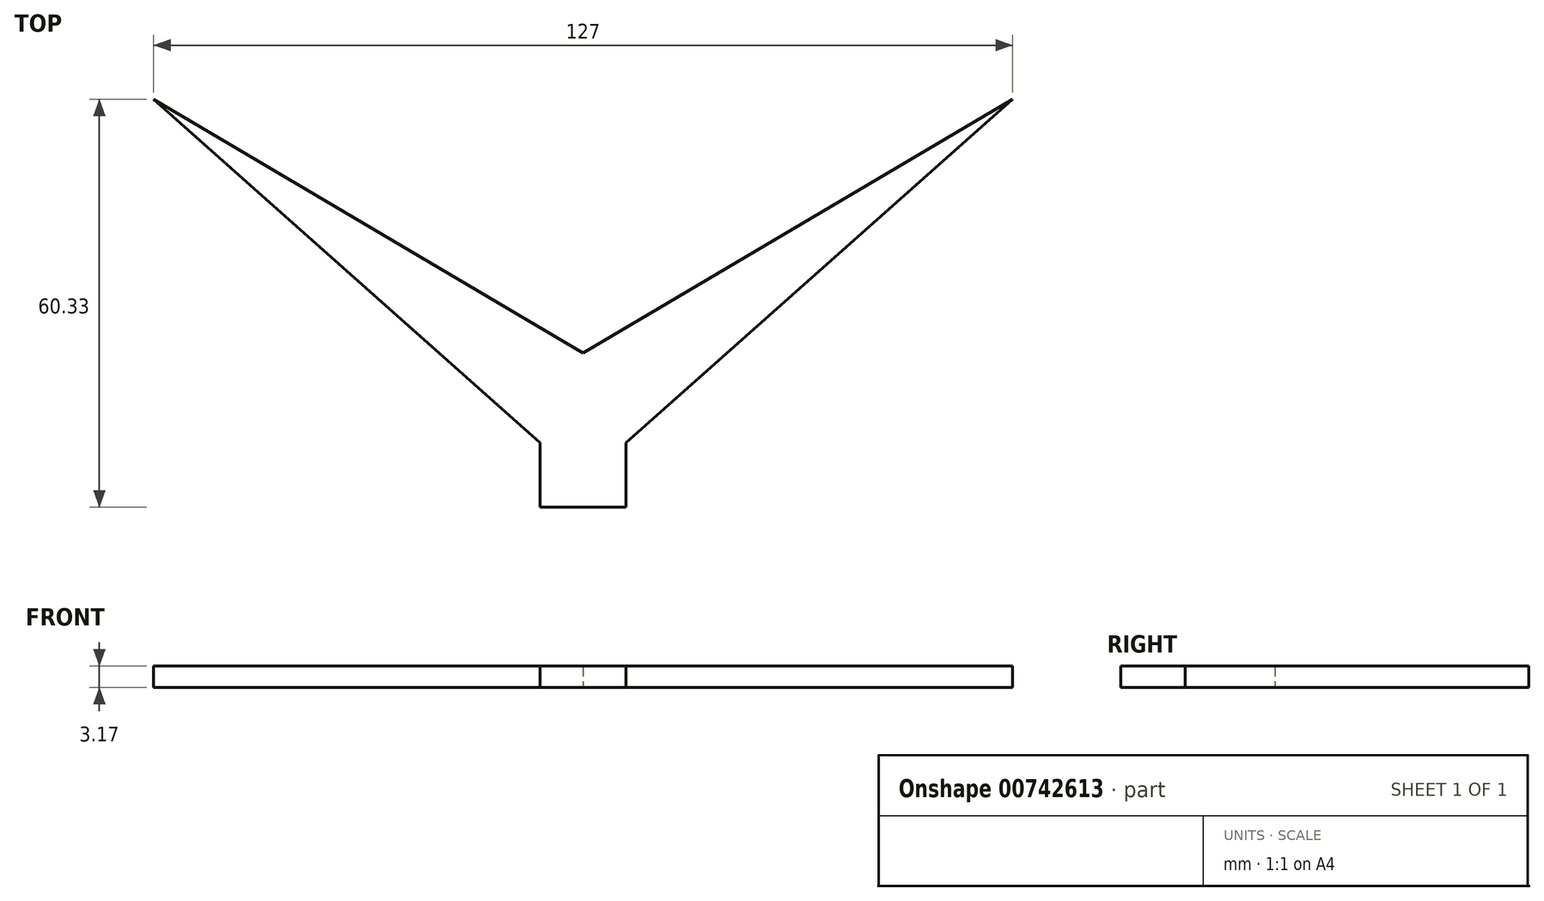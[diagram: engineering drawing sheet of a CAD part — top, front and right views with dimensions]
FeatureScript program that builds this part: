
annotation { "Feature Type Name" : "Feature", "Feature Type Description" : "" }
export const myFeature = defineFeature(function(context is Context, id is Id, definition is map)
    precondition{}
    {
        {
            var Q0;
            Q0=qCreatedBy(makeId("Top.planeOp"),FACE);
            var sketch = newSketch(context, id + "F0", { "sketchPlane" : qUnion([Q0])});
            skLineSegment(sketch, "E0.bottom", {"start": v(6.35, -9.52) * mm, "end": v(-6.35, -9.52) * mm});
            skLineSegment(sketch, "E0.top", {"start": v(6.35, 9.53) * mm, "end": v(-6.35, 9.53) * mm});
            skLineSegment(sketch, "E0.left", {"start": v(6.35, -9.52) * mm, "end": v(6.35, 9.53) * mm});
            skLineSegment(sketch, "E0.right", {"start": v(-6.35, -9.52) * mm, "end": v(-6.35, 9.53) * mm});
            skPoint(sketch, "E0.middle", {"position": v(0, 0) * mm});
            skLineSegment(sketch, "E1", {"start": v(-44.45, 50.8) * mm, "end": v(44.45, 50.8) * mm});
            skLineSegment(sketch, "E2.bottom", {"start": v(0, 0) * mm, "end": v(63.5, 0) * mm});
            skLineSegment(sketch, "E2.top", {"start": v(0, 50.8) * mm, "end": v(63.5, 50.8) * mm});
            skLineSegment(sketch, "E2.left", {"start": v(0, 0) * mm, "end": v(0, 50.8) * mm});
            skLineSegment(sketch, "E2.right", {"start": v(63.5, 0) * mm, "end": v(63.5, 50.8) * mm});
            skLineSegment(sketch, "E3.bottom", {"start": v(0, 0) * mm, "end": v(-63.5, 0) * mm});
            skLineSegment(sketch, "E3.top", {"start": v(0, 50.8) * mm, "end": v(-63.5, 50.8) * mm});
            skLineSegment(sketch, "E3.right", {"start": v(-63.5, 0) * mm, "end": v(-63.5, 50.8) * mm});
            skLineSegment(sketch, "E4", {"start": v(-63.5, 50.8) * mm, "end": v(6.35, 9.52) * mm});
            skLineSegment(sketch, "E5", {"start": v(-6.35, 9.52) * mm, "end": v(63.5, 50.8) * mm});
            skLineSegment(sketch, "E6", {"start": v(-6.35, 0) * mm, "end": v(-63.5, 50.8) * mm});
            skLineSegment(sketch, "E7", {"start": v(6.35, 0) * mm, "end": v(63.5, 50.8) * mm});
            skSolve(sketch);
        }
        {
            var Q0;
            {var subQ3=sQuery(id+"F0.wireOp",EDGE,"E7");Q0=makeQuery(id+"F0.imprint","IMPRINT",FACE,{"disambiguationData":[TD([[makeQuery(id+"F0.imprint","IMPRINT",EDGE,{"derivedFrom":subQ3}),1.0]])]});}
            var Q1;
            {var subQ3=sQuery(id+"F0.wireOp",EDGE,"E6");Q1=makeQuery(id+"F0.imprint","IMPRINT",FACE,{"disambiguationData":[TD([[makeQuery(id+"F0.imprint","IMPRINT",EDGE,{"derivedFrom":subQ3}),-1.0]])]});}
            var Q2;
            {var subQ1=sQuery(id+"F0.wireOp",EDGE,"E0.top");var subQ3=sQuery(id+"F0.wireOp",EDGE,"E2.left");var subQ4=makeQuery(id+"F0.imprint","INTERSECT",VERTEX,{"derivedFrom":[subQ1,subQ3]});Q2=makeQuery(id+"F0.imprint","IMPRINT",FACE,{"disambiguationData":[TD([[makeQuery(id+"F0.imprint","IMPRINT",EDGE,{"disambiguationData":[TD([[subQ4,1.0]])],"derivedFrom":subQ1}),-1.0]])]});}
            var Q3;
            {var subQ1=sQuery(id+"F0.wireOp",EDGE,"E0.top");var subQ3=sQuery(id+"F0.wireOp",EDGE,"E2.left");var subQ4=makeQuery(id+"F0.imprint","INTERSECT",VERTEX,{"derivedFrom":[subQ1,subQ3]});Q3=makeQuery(id+"F0.imprint","IMPRINT",FACE,{"disambiguationData":[TD([[makeQuery(id+"F0.imprint","IMPRINT",EDGE,{"disambiguationData":[TD([[subQ4,-1.0]])],"derivedFrom":subQ1}),-1.0]])]});}
            var Q4;
            {var subQ1=sQuery(id+"F0.wireOp",EDGE,"E0.top");var subQ3=sQuery(id+"F0.wireOp",EDGE,"E2.left");var subQ4=makeQuery(id+"F0.imprint","INTERSECT",VERTEX,{"derivedFrom":[subQ1,subQ3]});Q4=makeQuery(id+"F0.imprint","IMPRINT",FACE,{"disambiguationData":[TD([[makeQuery(id+"F0.imprint","IMPRINT",EDGE,{"disambiguationData":[TD([[subQ4,1.0]])],"derivedFrom":subQ1}),1.0]])]});}
            var Q5;
            {var subQ1=sQuery(id+"F0.wireOp",EDGE,"E0.top");var subQ3=sQuery(id+"F0.wireOp",EDGE,"E2.left");var subQ4=makeQuery(id+"F0.imprint","INTERSECT",VERTEX,{"derivedFrom":[subQ1,subQ3]});Q5=makeQuery(id+"F0.imprint","IMPRINT",FACE,{"disambiguationData":[TD([[makeQuery(id+"F0.imprint","IMPRINT",EDGE,{"disambiguationData":[TD([[subQ4,-1.0]])],"derivedFrom":subQ1}),1.0]])]});}
            var Q6;
            {var subQ5=sQuery(id+"F0.wireOp",EDGE,"E0.bottom");Q6=makeQuery(id+"F0.imprint","IMPRINT",FACE,{"disambiguationData":[TD([[makeQuery(id+"F0.imprint","IMPRINT",EDGE,{"derivedFrom":subQ5}),-1.0]])]});}
            extrude(context, id + "F1", {"entities" : qUnion([Q0, Q1, Q2, Q3, Q4, Q5, Q6]), "depth" : 3.17 * mm, "offsetDistance" : 25.4 * mm});
        }
    });
